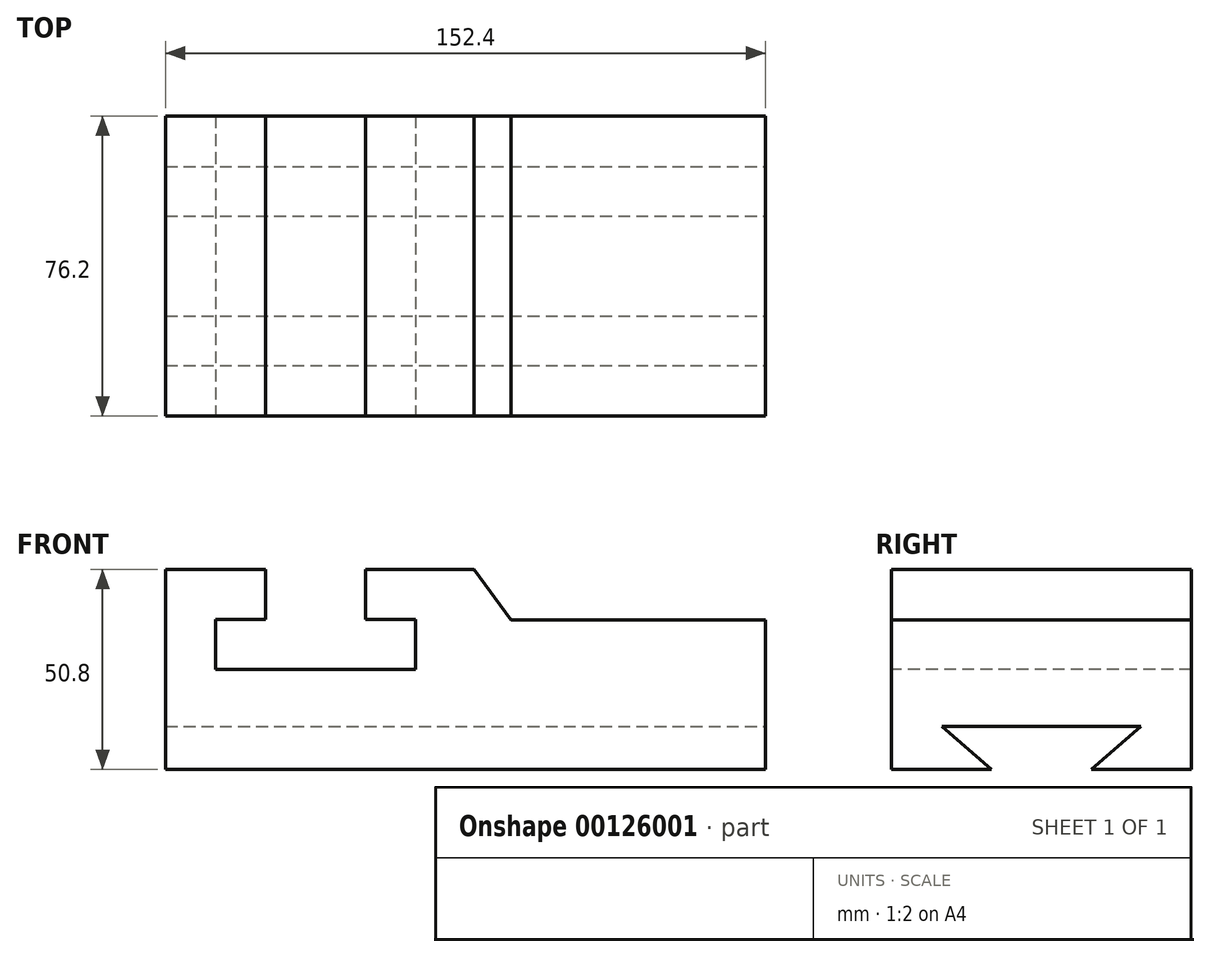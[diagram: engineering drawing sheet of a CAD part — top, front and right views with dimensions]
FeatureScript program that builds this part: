
annotation { "Feature Type Name" : "Feature", "Feature Type Description" : "" }
export const myFeature = defineFeature(function(context is Context, id is Id, definition is map)
    precondition{}
    {
        {
            var Q0;
            Q0=qCreatedBy(makeId("Top.planeOp"),FACE);
            var sketch = newSketch(context, id + "F0", { "sketchPlane" : qUnion([Q0])});
            skLineSegment(sketch, "E0", {"start": v(-78.37, 0) * mm, "end": v(-78.37, -38.1) * mm});
            skLineSegment(sketch, "E1", {"start": v(-78.37, -38.1) * mm, "end": v(74.03, -38.1) * mm});
            skLineSegment(sketch, "E2", {"start": v(74.03, -38.1) * mm, "end": v(74.03, 0) * mm});
            skLineSegment(sketch, "E3", {"start": v(74.03, 0) * mm, "end": v(-78.37, 0) * mm});
            skSolve(sketch);
        }
        {
            var Q0;
            Q0=makeQuery(id+"F0.imprint","IMPRINT",FACE,{"disambiguationData":[TD([[makeQuery(id+"F0.imprint","IMPRINT",EDGE,{"derivedFrom":sQuery(id+"F0.wireOp",EDGE,"E0")}),1.0]])]});
            extrude(context, id + "F1", {"entities" : qUnion([Q0]), "depth" : 50.8 * mm});
        }
        {
            var Q0;
            Q0=makeQuery(id+"F1.opExtrude","SWEPT_FACE",FACE,{"disambiguationData":[OSD([sQuery(id+"F0.wireOp",EDGE,"E2")])]});
            var sketch = newSketch(context, id + "F2", { "sketchPlane" : qUnion([Q0])});
            skLineSegment(sketch, "E4", {"start": v(0, 0) * mm, "end": v(-12.7, 0) * mm});
            skLineSegment(sketch, "E5", {"start": v(-25.33, 10.88) * mm, "end": v(-12.7, 0) * mm});
            skLineSegment(sketch, "E6", {"start": v(-25.33, 10.88) * mm, "end": v(0, 10.88) * mm});
            skLineSegment(sketch, "E7", {"start": v(0, 10.88) * mm, "end": v(0, 0) * mm});
            skLineSegment(sketch, "E8", {"start": v(-12.7, 0) * mm, "end": v(0, 0) * mm});
            skSolve(sketch);
        }
        {
            var Q0;
            Q0=makeQuery(id+"F2.imprint","IMPRINT",FACE,{"disambiguationData":[TD([[makeQuery(id+"F2.imprint","IMPRINT",EDGE,{"derivedFrom":sQuery(id+"F2.wireOp",EDGE,"E5")}),1.0]])]});
            extrude(context, id + "F3", {"entities" : qUnion([Q0]), "operationType" : NewBodyOperationType.REMOVE, "endBound" : BoundingType.THROUGH_ALL, "oppositeDirection" : true, "depth" : 25.4 * mm});
        }
        {
            var Q0;
            Q0=makeQuery(id+"F1.opExtrude","SWEPT_FACE",FACE,{"disambiguationData":[OSD([sQuery(id+"F0.wireOp",EDGE,"E1")])]});
            var sketch = newSketch(context, id + "F4", { "sketchPlane" : qUnion([Q0])});
            skLineSegment(sketch, "E9", {"start": v(-78.37, 50.8) * mm, "end": v(-52.97, 50.8) * mm});
            skLineSegment(sketch, "E10", {"start": v(-52.97, 50.8) * mm, "end": v(-52.97, 38.1) * mm});
            skLineSegment(sketch, "E11", {"start": v(-52.97, 38.1) * mm, "end": v(-65.67, 38.1) * mm});
            skLineSegment(sketch, "E12", {"start": v(-65.67, 38.1) * mm, "end": v(-65.67, 25.4) * mm});
            skPoint(sketch, "E12.endSnap0", {"position": v(-78.37, 25.4) * mm});
            skLineSegment(sketch, "E13", {"start": v(-65.67, 25.4) * mm, "end": v(-14.87, 25.4) * mm});
            skLineSegment(sketch, "E14", {"start": v(-14.87, 25.4) * mm, "end": v(-14.87, 38.1) * mm});
            skLineSegment(sketch, "E15", {"start": v(-14.87, 38.1) * mm, "end": v(-27.57, 38.1) * mm});
            skLineSegment(sketch, "E16", {"start": v(-27.57, 38.1) * mm, "end": v(-27.57, 50.8) * mm});
            skLineSegment(sketch, "E17", {"start": v(-52.97, 50.8) * mm, "end": v(-27.57, 50.8) * mm});
            skSolve(sketch);
        }
        {
            var Q0;
            Q0=makeQuery(id+"F4.imprint","IMPRINT",FACE,{"disambiguationData":[TD([[makeQuery(id+"F4.imprint","IMPRINT",EDGE,{"derivedFrom":sQuery(id+"F4.wireOp",EDGE,"E10")}),1.0]])]});
            extrude(context, id + "F5", {"entities" : qUnion([Q0]), "operationType" : NewBodyOperationType.REMOVE, "endBound" : BoundingType.THROUGH_ALL, "oppositeDirection" : true, "depth" : 25.4 * mm});
        }
        {
            var Q0;
            Q0=makeQuery(id+"F4.imprint","IMPRINT",FACE,{"disambiguationData":[TD([[makeQuery(id+"F4.imprint","IMPRINT",EDGE,{"derivedFrom":sQuery(id+"F4.wireOp",EDGE,"E9")}),-1.0]])]});
            var sketch = newSketch(context, id + "F6", { "sketchPlane" : qUnion([Q0])});
            skLineSegment(sketch, "E18", {"start": v(0, 50.8) * mm, "end": v(0, 50.8) * mm});
            skLineSegment(sketch, "E19", {"start": v(0, 50.8) * mm, "end": v(9.34, 38) * mm});
            skLineSegment(sketch, "E20", {"start": v(9.34, 38) * mm, "end": v(74.6, 38) * mm});
            skLineSegment(sketch, "E21", {"start": v(74.6, 38) * mm, "end": v(74.6, 50.8) * mm});
            skLineSegment(sketch, "E22", {"start": v(74.6, 50.8) * mm, "end": v(0, 50.8) * mm});
            skSolve(sketch);
        }
        {
            var Q0;
            Q0 = qSketchRegion(id + "F6", true);
            extrude(context, id + "F7", {"entities" : qUnion([Q0]), "operationType" : NewBodyOperationType.REMOVE, "endBound" : BoundingType.THROUGH_ALL, "oppositeDirection" : true, "depth" : 25.4 * mm});
        }
        {
            var Q0;
            Q0=makeQuery(id+"F1.opExtrude","SWEPT_BODY",BODY,{"disambiguationData":[OSD([sQuery(id+"F0.wireOp",EDGE,"E0"),sQuery(id+"F0.wireOp",EDGE,"E1"),sQuery(id+"F0.wireOp",EDGE,"E2"),sQuery(id+"F0.wireOp",EDGE,"E3")])]});
            var Q1;
            Q1=qCreatedBy(makeId("Front.planeOp"),FACE);
            mirror(context, id + "F8", {"operationType" : NewBodyOperationType.ADD, "entities" : qUnion([Q0]), "mirrorPlane" : qUnion([Q1])});
        }
    });
